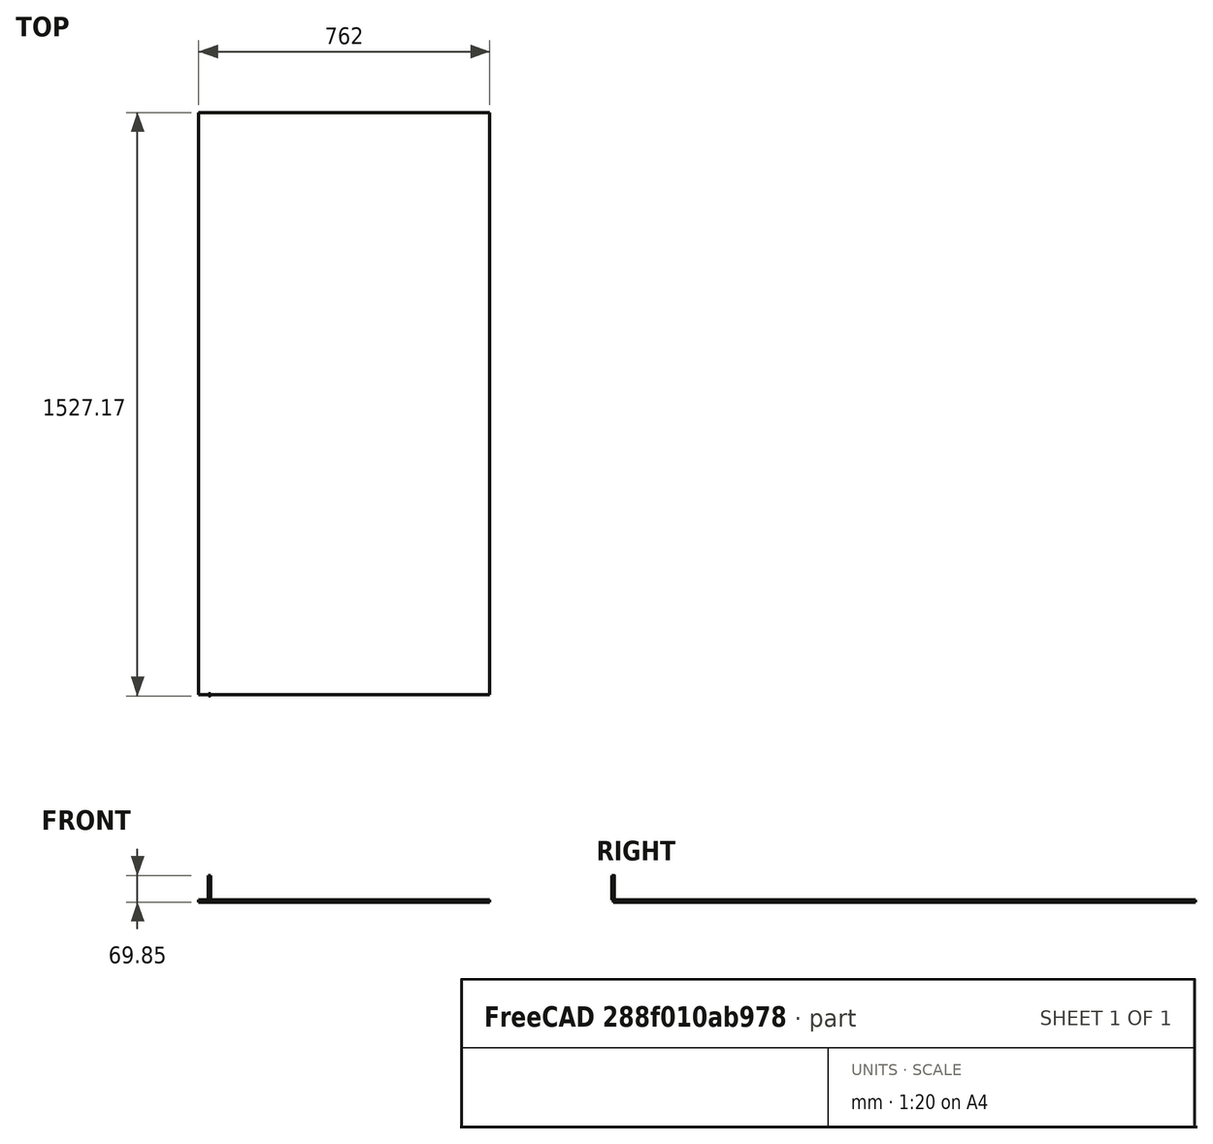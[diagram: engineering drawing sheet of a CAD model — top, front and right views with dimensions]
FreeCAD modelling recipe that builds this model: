
FCSTD DOCUMENT  (FreeCAD 0.21R33771 (Git))
Label: horizontal_panel
License: Creative Commons Attribution-NonCommercial-ShareAlike 4.0
LicenseURL: https://creativecommons.org/licenses/by-nc-sa/4.0/
objects: Part::Box×16, Part::FeaturePython×11, TechDraw::DrawViewDimension×10, Part::Cylinder×8, Path::FeaturePython×8, Part::Common×7, App::DocumentObjectGroup×3, Part::Cut×1, TechDraw::DrawSVGTemplate×1, App::FeaturePython×1, Part::MultiFuse×1, TechDraw::DrawViewPart×1, TechDraw::DrawPage×1
note: 65 computed .brp shape members not serialized (recipe doc carries the construction recipe); baked Part::Feature solids carry a one-line shape summary decoded from their .brp

FEATURE [Part::Box] cube
  AttacherType = Attacher::AttachEngine3D
  Height = 6.35
  Length = 628.65
  Width = 511.175
FEATURE [Part::Box] cube001
  AttacherType = Attacher::AttachEngine3D
  Height = 12.7
  Length = 501.65
  Width = 374.65
FEATURE [Part::Cylinder] cylinder
  Angle = 360
  AttacherType = Attacher::AttachEngine3D
  FirstAngle = 0
  Height = 12.7
  Radius = 31.75
  SecondAngle = 0
FEATURE [Part::FeaturePython] minkowski  # WARN: FeaturePython — macro-defined, semantics opaque (R4)
  Arguments = {'convexity': '0'}
  Children = -> [cube001,cylinder]
  Operation = minkowski
  Placement = pos=(63.5,73.025,-2.54) rot=(0,0,1;0rad)
FEATURE [Part::Cut] difference
  Base = -> cube
  Tool = -> minkowski
FEATURE [Part::Box] cube002
  AttacherType = Attacher::AttachEngine3D
  Height = 12.7
  Length = 38.1
  Width = 82.55
FEATURE [Part::Cylinder] cylinder001
  Angle = 360
  AttacherType = Attacher::AttachEngine3D
  FirstAngle = 0
  Height = 12.7
  Radius = 9.525
  SecondAngle = 0
FEATURE [Part::FeaturePython] minkowski001  # WARN: FeaturePython — macro-defined, semantics opaque (R4)
  Arguments = {'convexity': '0'}
  Children = -> [cube002,cylinder001]
  Operation = minkowski
  Placement = pos=(-19.05,9.525,0) rot=(0,0,1;0rad)
FEATURE [Part::Box] cube003
  AttacherType = Attacher::AttachEngine3D
  Height = 6.35
  Length = 28.575
  Placement = pos=(-28.575,0,12.7) rot=(0,0,1;0rad)
  Width = 101.6
FEATURE [Part::Common] intersection
  Base = -> minkowski001
  Placement = pos=(0,82.55,-12.7) rot=(0,0,1;0rad)
  Tool = -> cube003
FEATURE [Part::Box] cube004
  AttacherType = Attacher::AttachEngine3D
  Height = 12.7
  Length = 38.1
  Width = 82.55
FEATURE [Part::Cylinder] cylinder002
  Angle = 360
  AttacherType = Attacher::AttachEngine3D
  FirstAngle = 0
  Height = 12.7
  Radius = 9.525
  SecondAngle = 0
FEATURE [Part::FeaturePython] minkowski002  # WARN: FeaturePython — macro-defined, semantics opaque (R4)
  Arguments = {'convexity': '0'}
  Children = -> [cube004,cylinder002]
  Operation = minkowski
  Placement = pos=(-19.05,9.525,0) rot=(0,0,1;0rad)
FEATURE [Part::Box] cube005
  AttacherType = Attacher::AttachEngine3D
  Height = 6.35
  Length = 28.575
  Placement = pos=(-28.575,0,12.7) rot=(0,0,1;0rad)
  Width = 101.6
FEATURE [Part::Common] intersection001
  Base = -> minkowski002
  Placement = pos=(0,336.55,-12.7) rot=(0,0,1;0rad)
  Tool = -> cube005
FEATURE [Part::Box] cube006
  AttacherType = Attacher::AttachEngine3D
  Height = 12.7
  Length = 38.1
  Width = 82.55
FEATURE [Part::Cylinder] cylinder003
  Angle = 360
  AttacherType = Attacher::AttachEngine3D
  FirstAngle = 0
  Height = 12.7
  Radius = 9.525
  SecondAngle = 0
FEATURE [Part::FeaturePython] minkowski003  # WARN: FeaturePython — macro-defined, semantics opaque (R4)
  Arguments = {'convexity': '0'}
  Children = -> [cube006,cylinder003]
  Operation = minkowski
  Placement = pos=(-19.05,9.525,0) rot=(0,0,1;0rad)
FEATURE [Part::Box] cube007
  AttacherType = Attacher::AttachEngine3D
  Height = 6.35
  Length = 28.575
  Placement = pos=(-28.575,0,12.7) rot=(0,0,1;0rad)
  Width = 101.6
FEATURE [Part::Common] intersection002
  Base = -> minkowski003
  Placement = pos=(60.325,511.175,-12.7) rot=(0,0,-1;1.5708rad)
  Tool = -> cube007
FEATURE [Part::Box] cube008
  AttacherType = Attacher::AttachEngine3D
  Height = 12.7
  Length = 38.1
  Width = 82.55
FEATURE [Part::Cylinder] cylinder004
  Angle = 360
  AttacherType = Attacher::AttachEngine3D
  FirstAngle = 0
  Height = 12.7
  Radius = 9.525
  SecondAngle = 0
FEATURE [Part::FeaturePython] minkowski004  # WARN: FeaturePython — macro-defined, semantics opaque (R4)
  Arguments = {'convexity': '0'}
  Children = -> [cube008,cylinder004]
  Operation = minkowski
  Placement = pos=(-19.05,9.525,0) rot=(0,0,1;0rad)
FEATURE [Part::Box] cube009
  AttacherType = Attacher::AttachEngine3D
  Height = 6.35
  Length = 28.575
  Placement = pos=(-28.575,0,12.7) rot=(0,0,1;0rad)
  Width = 101.6
FEATURE [Part::Common] intersection003
  Base = -> minkowski004
  Placement = pos=(263.525,511.175,-12.7) rot=(0,0,-1;1.5708rad)
  Tool = -> cube009
FEATURE [Part::Box] cube010
  AttacherType = Attacher::AttachEngine3D
  Height = 12.7
  Length = 38.1
  Width = 82.55
FEATURE [Part::Cylinder] cylinder005
  Angle = 360
  AttacherType = Attacher::AttachEngine3D
  FirstAngle = 0
  Height = 12.7
  Radius = 9.525
  SecondAngle = 0
FEATURE [Part::FeaturePython] minkowski005  # WARN: FeaturePython — macro-defined, semantics opaque (R4)
  Arguments = {'convexity': '0'}
  Children = -> [cube010,cylinder005]
  Operation = minkowski
  Placement = pos=(-19.05,9.525,0) rot=(0,0,1;0rad)
FEATURE [Part::Box] cube011
  AttacherType = Attacher::AttachEngine3D
  Height = 6.35
  Length = 28.575
  Placement = pos=(-28.575,0,12.7) rot=(0,0,1;0rad)
  Width = 101.6
FEATURE [Part::Common] intersection004
  Base = -> minkowski005
  Placement = pos=(466.725,511.175,-12.7) rot=(0,0,-1;1.5708rad)
  Tool = -> cube011
FEATURE [Part::Box] cube012
  AttacherType = Attacher::AttachEngine3D
  Height = 12.7
  Length = 38.1
  Width = 82.55
FEATURE [Part::Cylinder] cylinder006
  Angle = 360
  AttacherType = Attacher::AttachEngine3D
  FirstAngle = 0
  Height = 12.7
  Radius = 9.525
  SecondAngle = 0
FEATURE [Part::FeaturePython] minkowski006  # WARN: FeaturePython — macro-defined, semantics opaque (R4)
  Arguments = {'convexity': '0'}
  Children = -> [cube012,cylinder006]
  Operation = minkowski
  Placement = pos=(-19.05,9.525,0) rot=(0,0,1;0rad)
FEATURE [Part::Box] cube013
  AttacherType = Attacher::AttachEngine3D
  Height = 6.35
  Length = 28.575
  Placement = pos=(-28.575,0,12.7) rot=(0,0,1;0rad)
  Width = 101.6
FEATURE [Part::Common] intersection005
  Base = -> minkowski006
  Placement = pos=(628.65,82.55,19.05) rot=(0,1,0;3.14159rad)
  Tool = -> cube013
FEATURE [Part::Box] cube014
  AttacherType = Attacher::AttachEngine3D
  Height = 12.7
  Length = 38.1
  Width = 82.55
FEATURE [Part::Cylinder] cylinder007
  Angle = 360
  AttacherType = Attacher::AttachEngine3D
  FirstAngle = 0
  Height = 12.7
  Radius = 9.525
  SecondAngle = 0
FEATURE [Part::FeaturePython] minkowski007  # WARN: FeaturePython — macro-defined, semantics opaque (R4)
  Arguments = {'convexity': '0'}
  Children = -> [cube014,cylinder007]
  Operation = minkowski
  Placement = pos=(-19.05,9.525,0) rot=(0,0,1;0rad)
FEATURE [Part::Box] cube015
  AttacherType = Attacher::AttachEngine3D
  Height = 6.35
  Length = 28.575
  Placement = pos=(-28.575,0,12.7) rot=(0,0,1;0rad)
  Width = 101.6
FEATURE [Part::Common] intersection006
  Base = -> minkowski007
  Placement = pos=(628.65,336.55,19.05) rot=(0,1,0;3.14159rad)
  Tool = -> cube015
FEATURE [TechDraw::DrawSVGTemplate] Template
  EditableTexts = Designed_by_Name=Designed by Name; Drawing_number=Drawing number; FC-Date=Date; FC-SC=Scale; FC-SH=Sheet; FC-Title=Title; Subtitle=Subtitle; Weight=Weight
  Height = 210
  Orientation = 1
  Template = <path>
  Width = 297
FEATURE [App::FeaturePython] SetupSheet  # Path/CAM operation (typed FeaturePython)
  ClearanceHeightExpression = OpStockZMax+SetupSheet.ClearanceHeightOffset
  ClearanceHeightOffset = 5
  CoolantMode = 0
  CoolantModes = None | Flood | Mist
  FinalDepthExpression = OpFinalDepth
  HorizRapid = 423.333
  SafeHeightExpression = OpStockZMax+SetupSheet.SafeHeightOffset
  SafeHeightOffset = 3
  StartDepthExpression = OpStartDepth
  StepDownExpression = OpToolDiameter
  VertRapid = 423.333
FEATURE [Part::FeaturePython] Stock001  # WARN: FeaturePython — macro-defined, semantics opaque (R4)
  Height = 6.35
  Length = 762
  Placement = pos=(-28.575,0,-6.35) rot=(0,0,1;0rad)
  StockType = CreateBox
  Width = 1524
FEATURE [Part::FeaturePython] ToolBit001  label="SpeTool 1/4" Downcut Carbide End Mill"  # Path/CAM toolbit (typed FeaturePython)
  BitPropertyNames = Chipload | CuttingEdgeHeight | Diameter | Flutes | Length | Material | ShankDiameter | SpindleDirection
  BitShape = <path>
  Chipload = 0
  CuttingEdgeHeight = 25.4
  Diameter = 6.35
  File = <userpath>/.config/FreeCAD-tools/Bit/1-4inch_endmill.fctb
  Flutes = 2
  Length = 63.5
  Material = 1
  ShankDiameter = 6.35
  ShapeName = endmill
  SpindleDirection = 0
FEATURE [Path::FeaturePython] SpeTool_1_4__Downcut_Carbide_End_Mill  label="SpeTool 1/4" Downcut Carbide End Mill001"  # Path/CAM operation (typed FeaturePython)
  HorizFeed = 42.3333
  HorizRapid = 423.333
  SpindleDir = 0
  SpindleSpeed = 12000
  Tool = -> ToolBit001
  ToolNumber = 2
  VertFeed = 12.7
  VertRapid = 423.333
  expr: HorizRapid = SetupSheet.HorizRapid
  expr: VertRapid = SetupSheet.VertRapid
FEATURE [App::DocumentObjectGroup] Tools
  Group = -> [SpeTool_1_4__Downcut_Carbide_End_Mill]
FEATURE [Part::MultiFuse] union
  Placement = pos=(0,0,-6.35) rot=(0,0,1;0rad)
  Shapes = -> [difference,intersection,intersection001,intersection002,intersection003,intersection004,intersection005,intersection006]
FEATURE [TechDraw::DrawViewPart] View  label="Horizontal Panel"
  CoarseView = false
  Direction = (0,0,1)
  Focus = 100
  HardHidden = false
  IsoCount = 0
  IsoHidden = false
  IsoVisible = true
  LockPosition = false
  Perspective = false
  Rotation = 0
  Scale = 0.25
  ScaleType = 0
  ScrubCount = 0
  SeamHidden = false
  SeamVisible = true
  SmoothHidden = false
  SmoothVisible = true
  Source = -> [union]
  X = 109.199
  XDirection = (1,0,0)
  Y = 127.087
FEATURE [TechDraw::DrawViewDimension] Dimension
  AngleOverride = false
  Arbitrary = false
  ArbitraryTolerances = false
  EqualTolerance = true
  ExtensionAngle = 0
  FormatSpec = %.3f
  FormatSpecOverTolerance = %+.3f
  FormatSpecUnderTolerance = %+.3f
  Inverted = false
  LineAngle = 0
  LockPosition = false
  MeasureType = 1
  OverTolerance = 0
  References2D = -> [View]
  Rotation = 0
  Scale = 0.25
  ScaleType = 0
  TheoreticalExact = false
  Type = 0
  UnderTolerance = 0
  X = -61.5051
  Y = -101.617
FEATURE [TechDraw::DrawViewDimension] Dimension001
  AngleOverride = false
  Arbitrary = false
  ArbitraryTolerances = false
  EqualTolerance = true
  ExtensionAngle = 0
  FormatSpec = %.3f
  FormatSpecOverTolerance = %+.3f
  FormatSpecUnderTolerance = %+.3f
  Inverted = false
  LineAngle = 0
  LockPosition = false
  MeasureType = 1
  OverTolerance = 0
  References2D = -> [View]
  Rotation = 0
  Scale = 0.25
  ScaleType = 0
  TheoreticalExact = false
  Type = 0
  UnderTolerance = 0
  X = 128.933
  Y = 0.521522
FEATURE [TechDraw::DrawViewDimension] Dimension002
  AngleOverride = false
  Arbitrary = false
  ArbitraryTolerances = false
  EqualTolerance = true
  ExtensionAngle = 0
  FormatSpec = %.3f
  FormatSpecOverTolerance = %+.3f
  FormatSpecUnderTolerance = %+.3f
  Inverted = false
  LineAngle = 0
  LockPosition = false
  MeasureType = 1
  OverTolerance = 0
  References2D = -> [View]
  Rotation = 0
  Scale = 0.25
  ScaleType = 0
  TheoreticalExact = false
  Type = 0
  UnderTolerance = 0
  X = 93.9443
  Y = -48.3236
FEATURE [TechDraw::DrawViewDimension] Dimension003
  AngleOverride = false
  Arbitrary = false
  ArbitraryTolerances = false
  EqualTolerance = true
  ExtensionAngle = 0
  FormatSpec = %.3f
  FormatSpecOverTolerance = %+.3f
  FormatSpecUnderTolerance = %+.3f
  Inverted = false
  LineAngle = 0
  LockPosition = false
  MeasureType = 1
  OverTolerance = 0
  References2D = -> [View]
  Rotation = 0
  Scale = 0.25
  ScaleType = 0
  TheoreticalExact = false
  Type = 0
  UnderTolerance = 0
  X = -90.4388
  Y = -51.5104
FEATURE [TechDraw::DrawViewDimension] Dimension004
  AngleOverride = false
  Arbitrary = false
  ArbitraryTolerances = false
  EqualTolerance = true
  ExtensionAngle = 0
  FormatSpec = %.3f
  FormatSpecOverTolerance = %+.3f
  FormatSpecUnderTolerance = %+.3f
  Inverted = false
  LineAngle = 0
  LockPosition = false
  MeasureType = 1
  OverTolerance = 0
  References2D = -> [View]
  Rotation = 0
  Scale = 0.25
  ScaleType = 0
  TheoreticalExact = false
  Type = 0
  UnderTolerance = 0
  X = -56.4478
  Y = 8.79311
FEATURE [TechDraw::DrawViewDimension] Dimension005
  AngleOverride = false
  Arbitrary = false
  ArbitraryTolerances = false
  EqualTolerance = true
  ExtensionAngle = 0
  FormatSpec = %.3f
  FormatSpecOverTolerance = %+.3f
  FormatSpecUnderTolerance = %+.3f
  Inverted = false
  LineAngle = 0
  LockPosition = false
  MeasureType = 1
  OverTolerance = 0
  References2D = -> [View]
  Rotation = 0
  Scale = 0.25
  ScaleType = 0
  TheoreticalExact = false
  Type = 0
  UnderTolerance = 0
  X = -30.0802
  Y = -38.7753
FEATURE [TechDraw::DrawViewDimension] Dimension006
  AngleOverride = false
  Arbitrary = false
  ArbitraryTolerances = false
  EqualTolerance = true
  ExtensionAngle = 0
  FormatSpec = %.3f
  FormatSpecOverTolerance = %+.3f
  FormatSpecUnderTolerance = %+.3f
  Inverted = false
  LineAngle = 0
  LockPosition = false
  MeasureType = 1
  OverTolerance = 0
  References2D = -> [View]
  Rotation = 0
  Scale = 0.25
  ScaleType = 0
  TheoreticalExact = false
  Type = 0
  UnderTolerance = 0
  X = -27.0878
  Y = -14.2365
FEATURE [TechDraw::DrawViewDimension] Dimension007
  AngleOverride = false
  Arbitrary = false
  ArbitraryTolerances = false
  EqualTolerance = true
  ExtensionAngle = 0
  FormatSpec = %.3f
  FormatSpecOverTolerance = %+.3f
  FormatSpecUnderTolerance = %+.3f
  Inverted = false
  LineAngle = 0
  LockPosition = false
  MeasureType = 1
  OverTolerance = 0
  References2D = -> [View]
  Rotation = 0
  Scale = 0.25
  ScaleType = 0
  TheoreticalExact = false
  Type = 0
  UnderTolerance = 0
  X = 24.0954
  Y = 5.53629
FEATURE [TechDraw::DrawViewDimension] Dimension008
  AngleOverride = false
  Arbitrary = false
  ArbitraryTolerances = false
  EqualTolerance = true
  ExtensionAngle = 0
  FormatSpec = %.3f
  FormatSpecOverTolerance = %+.3f
  FormatSpecUnderTolerance = %+.3f
  Inverted = false
  LineAngle = 0
  LockPosition = false
  MeasureType = 1
  OverTolerance = 0
  References2D = -> [View]
  Rotation = 0
  Scale = 0.25
  ScaleType = 0
  TheoreticalExact = false
  Type = 0
  UnderTolerance = 0
  X = 85.3152
  Y = -5.49954
FEATURE [TechDraw::DrawViewDimension] Dimension009
  AngleOverride = false
  Arbitrary = false
  ArbitraryTolerances = false
  EqualTolerance = true
  ExtensionAngle = 0
  FormatSpec = %.3f
  FormatSpecOverTolerance = %+.3f
  FormatSpecUnderTolerance = %+.3f
  Inverted = false
  LineAngle = 0
  LockPosition = false
  MeasureType = 1
  OverTolerance = 0
  References2D = -> [View]
  Rotation = 0
  Scale = 0.25
  ScaleType = 0
  TheoreticalExact = false
  Type = 0
  UnderTolerance = 0
  X = 108.218
  Y = -52.7375
FEATURE [TechDraw::DrawPage] Page
  KeepUpdated = true
  NextBalloonIndex = 1
  ProjectionType = 0
  Scale = 0.25
  Template = -> Template
  Views = -> [View,Dimension,Dimension001,Dimension002,Dimension003,Dimension004,Dimension005,Dimension006,Dimension007,Dimension008,Dimension009]
FEATURE [Part::FeaturePython] Clone  label="Model-union"  # Draft clone (typed FeaturePython)
  AttacherType = Attacher::AttachEngine3D
  Fuse = false
  Objects = -> [union]
  PathResource = Model
  Placement = pos=(38.1,22.125,-6.35) rot=(0,0,1;0rad)
  Scale = (1,1,1)
FEATURE [App::DocumentObjectGroup] Model
  Group = -> [Clone]
FEATURE [Path::FeaturePython] Profile  label="ProfileOutside"  # Path/CAM operation (typed FeaturePython)
  Active = true
  AreaParams:
    Tolerance = 1e-07
    FitArcs = True
    Simplify = False
    CleanDistance = 0.0
    Accuracy = 0.01
    Unit = 1.0
    MinArcPoints = 4
    MaxArcPoints = 100
    ClipperScale = 10000000.0
    Fill = 0
    Coplanar = 0
    Reorient = True
    Outline = False
    Explode = False
    OpenMode = 0
    Deflection = 0.01
    SubjectFill = 0
    ClipFill = 0
    Offset = 3.175
    ExtraPass = 0
    Stepover = 0.0
    LastStepover = 0.0
    JoinType = 0
    EndType = 0
    MiterLimit = 2.0
    RoundPrecision = 0.0
    PocketMode = 0
    ToolRadius = 1.0
    PocketExtraOffset = 0.0
    PocketStepover = 0.0
    PocketLastStepover = 0.0
    FromCenter = False
    Angle = 45.0
    AngleShift = 0.0
    Shift = 0.0
    Thicken = False
    SectionCount = -1
    Stepdown = 1.0
    SectionOffset = 0.0
    SectionTolerance = 1e-07
    SectionMode = 2
    Project = False
  Base = -> [Clone]
  ClearanceHeight = 5
  CoolantMode = 0
  CycleTime = 00:01:00
  Direction = 0
  FinalDepth = -6.35
  HandleMultipleFeatures = 0
  JoinType = 0
  MiterLimit = 0.1
  OffsetExtra = 0
  OpFinalDepth = -6.35
  OpStartDepth = 0
  OpStockZMax = 0
  OpStockZMin = -6.35
  OpToolDiameter = 6.35
  PathParams = {'orientation': 1, 'feedrate': 42.333333333333336, 'feedrate_v': 12.7, 'verbose': True, 'resume_height': 3.0, 'retraction': 5.0, 'return_end': True, 'preamble': False, 'start': Vector (0.0, 0.0, 0.0)}
  SafeHeight = 3
  Side = 0
  SplitArcs = false
  StartDepth = 0
  StartPoint = (0,0,0)
  StepDown = 6.35
  ToolController = -> SpeTool_1_4__Downcut_Carbide_End_Mill
  UseComp = true
  UseStartPoint = true
  processCircles = false
  processHoles = false
  processPerimeter = true
  expr: ClearanceHeight = OpStockZMax + SetupSheet.ClearanceHeightOffset
  expr: FinalDepth = OpFinalDepth
  expr: SafeHeight = OpStockZMax + SetupSheet.SafeHeightOffset
  expr: StartDepth = OpStartDepth
  expr: StepDown = OpToolDiameter
FEATURE [Path::FeaturePython] Profile001  label="Cutout"  # Path/CAM operation (typed FeaturePython)
  Active = true
  AreaParams:
    Tolerance = 1e-07
    FitArcs = True
    Simplify = False
    CleanDistance = 0.0
    Accuracy = 0.01
    Unit = 1.0
    MinArcPoints = 4
    MaxArcPoints = 100
    ClipperScale = 10000000.0
    Fill = 0
    Coplanar = 0
    Reorient = True
    Outline = False
    Explode = False
    OpenMode = 0
    Deflection = 0.01
    SubjectFill = 0
    ClipFill = 0
    Offset = -3.175
    ExtraPass = 0
    Stepover = 0.0
    LastStepover = 0.0
    JoinType = 0
    EndType = 0
    MiterLimit = 2.0
    RoundPrecision = 0.0
    PocketMode = 0
    ToolRadius = 1.0
    PocketExtraOffset = 0.0
    PocketStepover = 0.0
    PocketLastStepover = 0.0
    FromCenter = False
    Angle = 45.0
    AngleShift = 0.0
    Shift = 0.0
    Thicken = False
    SectionCount = -1
    Stepdown = 1.0
    SectionOffset = 0.0
    SectionTolerance = 1e-07
    SectionMode = 2
    Project = False
  Base = -> [Clone]
  ClearanceHeight = 5
  CoolantMode = 0
  CycleTime = 00:00:45
  Direction = 0
  FinalDepth = -6.35
  HandleMultipleFeatures = 0
  JoinType = 0
  MiterLimit = 0.1
  OffsetExtra = 0
  OpFinalDepth = -6.35
  OpStartDepth = 0
  OpStockZMax = 0
  OpStockZMin = -6.35
  OpToolDiameter = 6.35
  PathParams = {'orientation': 1, 'feedrate': 42.333333333333336, 'feedrate_v': 12.7, 'verbose': True, 'resume_height': 3.0, 'retraction': 5.0, 'return_end': True, 'preamble': False, 'start': Vector (0.0, 0.0, 0.0)}
  SafeHeight = 3
  Side = 1
  SplitArcs = false
  StartDepth = 0
  StartPoint = (0,0,0)
  StepDown = 6.35
  ToolController = -> SpeTool_1_4__Downcut_Carbide_End_Mill
  UseComp = true
  UseStartPoint = true
  processCircles = false
  processHoles = false
  processPerimeter = true
  expr: ClearanceHeight = OpStockZMax + SetupSheet.ClearanceHeightOffset
  expr: FinalDepth = OpFinalDepth
  expr: SafeHeight = OpStockZMax + SetupSheet.SafeHeightOffset
  expr: StartDepth = OpStartDepth
  expr: StepDown = OpToolDiameter
FEATURE [Path::FeaturePython] DressupTag001  # Path/CAM operation (typed FeaturePython)
  Angle = 45
  Base = -> Profile001
  Height = 3.175
  Positions = (4) [(478.194,66.5849,0),(226.656,66.5849,0),(226.656,498.365,0),(478.194,498.365,0)]
  Radius = 0
  SegmentationFactor = 50
  Width = 50.3072
FEATURE [Path::FeaturePython] RampEntryDressup001  label="RampEntryCutout"  # Path/CAM operation (typed FeaturePython)
  Angle = 60
  Base = -> DressupTag001
  CustomFeedRate = 0
  DressupStartDepth = 0
  Method = 2
  RampFeedRate = 0
  UseStartDepth = false
FEATURE [Path::FeaturePython] DressupTag  # Path/CAM operation (typed FeaturePython)
  Angle = 45
  Base = -> Profile
  Height = 3.175
  Positions = (4) [(352.425,18.95,0),(34.925,282.474,0),(669.925,318.99,0),(669.925,245.961,0)]
  Radius = 0
  SegmentationFactor = 50
  Width = 62.865
FEATURE [Path::FeaturePython] RampEntryDressup  label="RampEntryOutside"  # Path/CAM operation (typed FeaturePython)
  Angle = 60
  Base = -> DressupTag
  CustomFeedRate = 0
  DressupStartDepth = 0
  Method = 2
  RampFeedRate = 0
  UseStartDepth = false
FEATURE [App::DocumentObjectGroup] Operations
  Group = -> [RampEntryDressup001,RampEntryDressup]
FEATURE [Path::FeaturePython] Job  label="HorizontalPanelJob"  # Path/CAM operation (typed FeaturePython)
  CycleTime = 00:01:45
  Fixtures = G54
  GeometryTolerance = 0
  JobType = 0
  LastPostProcessDate = 2024-07-14 17:30:56.343990
  LastPostProcessOutput = <userpath>/GIT/cnc-projects/shophacks_ultimate_air_filter/horizontal_panel.gcode
  Model = -> Model
  Operations = -> Operations
  OrderOutputBy = 0
  PostProcessor = 14
  PostProcessorArgs = --inches
  PostProcessorOutputFile = <userpath>/.config/FreeCAD-tools/Bit/horizontal_panel.gcode
  SetupSheet = -> SetupSheet
  SplitOutput = false
  Stock = -> Stock001
  Tools = -> Tools
note: 2 file-system paths scrubbed to <path> (originals preserved in the JSON sidecar)
